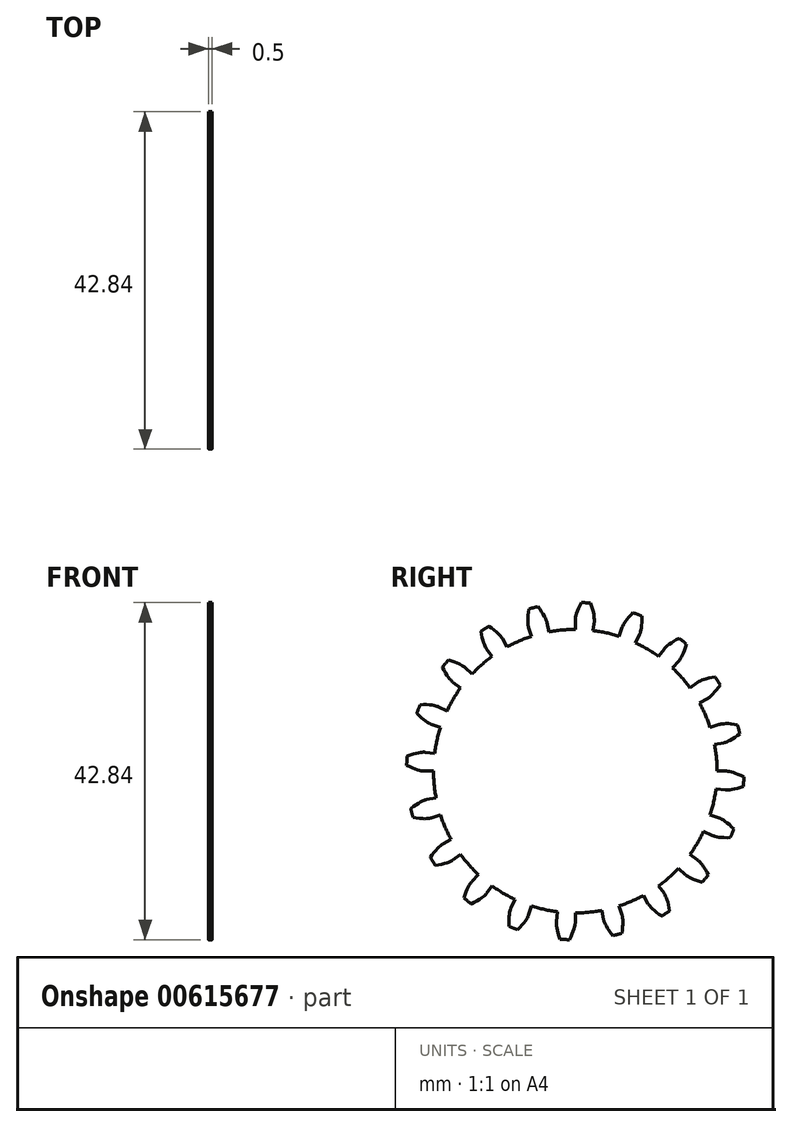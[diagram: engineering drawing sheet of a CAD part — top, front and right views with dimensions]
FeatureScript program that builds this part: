
annotation { "Feature Type Name" : "Feature", "Feature Type Description" : "" }
export const myFeature = defineFeature(function(context is Context, id is Id, definition is map)
    precondition{}
    {
        {
            assignVariable(context, id + "F0", {"name" : "GearThickness", "anyValue" : .5});
        }
        {
            var Q0;
            Q0=qCreatedBy(makeId("Right.planeOp"),FACE);
            var sketch = newSketch(context, id + "F1", { "sketchPlane" : qUnion([Q0])});
            skCircle(sketch, "E0", {"center": v(0, 0) * mm, "radius": 18 * mm});
            skCircle(sketch, "E1", {"center": v(0, 0) * mm, "radius": 19.21 * mm, "construction": true});
            skCircle(sketch, "E2", {"center": v(0, 0) * mm, "radius": 19.84 * mm, "construction": true});
            skCircle(sketch, "E3", {"center": v(0, 0) * mm, "radius": 21.43 * mm});
            skLineSegment(sketch, "E4", {"start": v(0, 0) * mm, "end": v(-19.21, 0) * mm, "construction": true});
            skLineSegment(sketch, "E5.1.0", {"start": v(0, 0) * mm, "end": v(-19.19, 0.96) * mm, "construction": true});
            skLineSegment(sketch, "E5.2.0", {"start": v(0, 0) * mm, "end": v(-19.12, 1.92) * mm, "construction": true});
            skLineSegment(sketch, "E5.3.0", {"start": v(0, 0) * mm, "end": v(-19, 2.87) * mm, "construction": true});
            skLineSegment(sketch, "E5.4.0", {"start": v(0, 0) * mm, "end": v(-18.83, 3.82) * mm, "construction": true});
            skLineSegment(sketch, "E5.5.0", {"start": v(0, 0) * mm, "end": v(-18.61, 4.75) * mm, "construction": true});
            skLineSegment(sketch, "E5.6.0", {"start": v(0, 0) * mm, "end": v(-18.35, 5.68) * mm, "construction": true});
            skLineSegment(sketch, "E5.7.0", {"start": v(0, 0) * mm, "end": v(-18.05, 6.59) * mm, "construction": true});
            skLineSegment(sketch, "E5.8.0", {"start": v(0, 0) * mm, "end": v(-17.7, 7.48) * mm, "construction": true});
            skLineSegment(sketch, "E5.9.0", {"start": v(0, 0) * mm, "end": v(-17.3, 8.36) * mm, "construction": true});
            skLineSegment(sketch, "E5.10.0", {"start": v(0, 0) * mm, "end": v(-16.86, 9.21) * mm, "construction": true});
            skLineSegment(sketch, "E5.11.0", {"start": v(0, 0) * mm, "end": v(-16.38, 10.04) * mm, "construction": true});
            skLineSegment(sketch, "E5.12.0", {"start": v(0, 0) * mm, "end": v(-15.86, 10.85) * mm, "construction": true});
            skLineSegment(sketch, "E5.13.0", {"start": v(0, 0) * mm, "end": v(-15.3, 11.63) * mm, "construction": true});
            skLineSegment(sketch, "E5.14.0", {"start": v(0, 0) * mm, "end": v(-14.7, 12.38) * mm, "construction": true});
            skLineSegment(sketch, "E5.anchor2", {"start": v(0, 0) * mm, "end": v(-14.7, 12.38) * mm, "construction": true});
            skLineSegment(sketch, "E6", {"start": v(-19.19, 0.96) * mm, "end": v(-19.24, 0) * mm, "construction": true});
            skLineSegment(sketch, "E7", {"start": v(-19.12, 1.92) * mm, "end": v(-19.3, 0) * mm, "construction": true});
            skLineSegment(sketch, "E8", {"start": v(-19, 2.87) * mm, "end": v(-19.43, 0.02) * mm, "construction": true});
            skLineSegment(sketch, "E9", {"start": v(-18.61, 4.75) * mm, "end": v(-19.8, 0.1) * mm, "construction": true});
            skLineSegment(sketch, "E10", {"start": v(-18.35, 5.68) * mm, "end": v(-20.06, 0.17) * mm, "construction": true});
            skLineSegment(sketch, "E11", {"start": v(-18.05, 6.59) * mm, "end": v(-20.35, 0.27) * mm, "construction": true});
            skLineSegment(sketch, "E12", {"start": v(-17.7, 7.48) * mm, "end": v(-20.69, 0.4) * mm, "construction": true});
            skLineSegment(sketch, "E13", {"start": v(-17.3, 8.36) * mm, "end": v(-21.06, 0.57) * mm, "construction": true});
            skLineSegment(sketch, "E14", {"start": v(-16.86, 9.21) * mm, "end": v(-21.47, 0.78) * mm, "construction": true});
            skLineSegment(sketch, "E15", {"start": v(-16.38, 10.04) * mm, "end": v(-21.9, 1.03) * mm, "construction": true});
            skLineSegment(sketch, "E16", {"start": v(-18.83, 3.82) * mm, "end": v(-19.6, 0.05) * mm, "construction": true});
            skLineSegment(sketch, "E17", {"start": v(-15.86, 10.85) * mm, "end": v(-22.36, 1.33) * mm, "construction": true});
            skLineSegment(sketch, "E18", {"start": v(-15.3, 11.63) * mm, "end": v(-22.85, 1.69) * mm, "construction": true});
            skLineSegment(sketch, "E19", {"start": v(-14.7, 12.38) * mm, "end": v(-23.36, 2.1) * mm, "construction": true});
            skLineSegment(sketch, "E20", {"start": v(0, 0) * mm, "end": v(-19.17, 1.2) * mm, "construction": true});
            skLineSegment(sketch, "E21", {"start": v(-18, 0) * mm, "end": v(-19.21, 0) * mm});
            skLineSegment(sketch, "E22.MirrorCS", {"start": v(-17.87, 2.26) * mm, "end": v(-19.06, 2.4) * mm});
            skLineSegment(sketch, "E23", {"start": v(-19.21, 0) * mm, "end": v(-19.24, 0) * mm});
            skLineSegment(sketch, "E24", {"start": v(-19.24, 0) * mm, "end": v(-19.3, 0) * mm});
            skLineSegment(sketch, "E25", {"start": v(-19.3, 0) * mm, "end": v(-19.43, 0.02) * mm});
            skLineSegment(sketch, "E26", {"start": v(-19.43, 0.02) * mm, "end": v(-19.6, 0.05) * mm});
            skLineSegment(sketch, "E27", {"start": v(-19.6, 0.05) * mm, "end": v(-19.8, 0.1) * mm});
            skLineSegment(sketch, "E28", {"start": v(-19.8, 0.1) * mm, "end": v(-20.06, 0.17) * mm});
            skLineSegment(sketch, "E29", {"start": v(-20.06, 0.17) * mm, "end": v(-20.35, 0.27) * mm});
            skLineSegment(sketch, "E30", {"start": v(-20.35, 0.27) * mm, "end": v(-20.69, 0.4) * mm});
            skLineSegment(sketch, "E31", {"start": v(-20.69, 0.4) * mm, "end": v(-21.06, 0.57) * mm});
            skLineSegment(sketch, "E32", {"start": v(-21.06, 0.57) * mm, "end": v(-21.47, 0.78) * mm});
            skLineSegment(sketch, "E33", {"start": v(-21.47, 0.78) * mm, "end": v(-21.9, 1.03) * mm});
            skLineSegment(sketch, "E34", {"start": v(-21.9, 1.03) * mm, "end": v(-22.36, 1.33) * mm});
            skLineSegment(sketch, "E35", {"start": v(-22.36, 1.33) * mm, "end": v(-22.85, 1.69) * mm});
            skLineSegment(sketch, "E36", {"start": v(-22.85, 1.69) * mm, "end": v(-23.36, 2.1) * mm});
            skLineSegment(sketch, "E37.MirrorCS", {"start": v(-19.06, 2.4) * mm, "end": v(-19.08, 2.41) * mm});
            skLineSegment(sketch, "E38.MirrorCS", {"start": v(-19.08, 2.41) * mm, "end": v(-19.16, 2.41) * mm});
            skLineSegment(sketch, "E39.MirrorCS", {"start": v(-19.16, 2.41) * mm, "end": v(-19.28, 2.41) * mm});
            skLineSegment(sketch, "E40.MirrorCS", {"start": v(-19.28, 2.41) * mm, "end": v(-19.44, 2.4) * mm});
            skLineSegment(sketch, "E41.MirrorCS", {"start": v(-19.66, 2.38) * mm, "end": v(-19.92, 2.34) * mm});
            skLineSegment(sketch, "E42.MirrorCS", {"start": v(-19.92, 2.34) * mm, "end": v(-20.23, 2.28) * mm});
            skLineSegment(sketch, "E43.MirrorCS", {"start": v(-20.23, 2.28) * mm, "end": v(-20.58, 2.2) * mm});
            skLineSegment(sketch, "E44.MirrorCS", {"start": v(-20.58, 2.2) * mm, "end": v(-20.97, 2.07) * mm});
            skLineSegment(sketch, "E45.MirrorCS", {"start": v(-21.4, 1.92) * mm, "end": v(-21.86, 1.72) * mm});
            skLineSegment(sketch, "E46.MirrorCS", {"start": v(-20.97, 2.07) * mm, "end": v(-21.4, 1.92) * mm});
            skLineSegment(sketch, "E47.MirrorCS", {"start": v(-21.86, 1.72) * mm, "end": v(-22.36, 1.48) * mm});
            skLineSegment(sketch, "E48.MirrorCS", {"start": v(-22.36, 1.48) * mm, "end": v(-22.88, 1.2) * mm});
            skLineSegment(sketch, "E49.MirrorCS", {"start": v(-22.88, 1.2) * mm, "end": v(-23.44, 0.85) * mm});
            skLineSegment(sketch, "E50.MirrorCS", {"start": v(-19.44, 2.4) * mm, "end": v(-19.66, 2.38) * mm});
            skLineSegment(sketch, "E51.1.0", {"start": v(-17.13, -5.56) * mm, "end": v(-18.27, -5.94) * mm});
            skLineSegment(sketch, "E51.1.1", {"start": v(-21.32, -5.12) * mm, "end": v(-21.72, -5.5) * mm});
            skLineSegment(sketch, "E51.1.2", {"start": v(-17.69, -3.37) * mm, "end": v(-18.87, -3.6) * mm});
            skLineSegment(sketch, "E51.1.3", {"start": v(-20.94, -4.79) * mm, "end": v(-21.32, -5.12) * mm});
            skLineSegment(sketch, "E51.1.4", {"start": v(-20.66, -5.9) * mm, "end": v(-21.15, -5.78) * mm});
            skLineSegment(sketch, "E51.1.5", {"start": v(-21.15, -5.78) * mm, "end": v(-21.68, -5.64) * mm});
            skLineSegment(sketch, "E51.1.6", {"start": v(-20.58, -4.5) * mm, "end": v(-20.94, -4.79) * mm});
            skLineSegment(sketch, "E51.1.7", {"start": v(-22.13, -5.94) * mm, "end": v(-22.55, -6.43) * mm});
            skLineSegment(sketch, "E51.1.8", {"start": v(-20.25, -4.27) * mm, "end": v(-20.58, -4.5) * mm});
            skLineSegment(sketch, "E51.1.9", {"start": v(-22.25, -5.46) * mm, "end": v(-22.86, -5.23) * mm});
            skLineSegment(sketch, "E51.1.10", {"start": v(-21.72, -5.5) * mm, "end": v(-22.13, -5.94) * mm});
            skLineSegment(sketch, "E51.1.11", {"start": v(-20.2, -5.96) * mm, "end": v(-20.66, -5.9) * mm});
            skLineSegment(sketch, "E51.1.12", {"start": v(-21.68, -5.64) * mm, "end": v(-22.25, -5.46) * mm});
            skLineSegment(sketch, "E51.1.13", {"start": v(-19.43, -3.8) * mm, "end": v(-19.67, -3.93) * mm});
            skLineSegment(sketch, "E51.1.14", {"start": v(-19.67, -3.93) * mm, "end": v(-19.94, -4.08) * mm});
            skLineSegment(sketch, "E51.1.15", {"start": v(-19.94, -4.08) * mm, "end": v(-20.25, -4.27) * mm});
            skLineSegment(sketch, "E51.1.16", {"start": v(-19.44, -6.03) * mm, "end": v(-19.8, -6) * mm});
            skLineSegment(sketch, "E51.1.17", {"start": v(-19.13, -6.03) * mm, "end": v(-19.44, -6.03) * mm});
            skLineSegment(sketch, "E51.1.18", {"start": v(-19.8, -6) * mm, "end": v(-20.2, -5.96) * mm});
            skLineSegment(sketch, "E51.1.19", {"start": v(-19.24, -3.72) * mm, "end": v(-19.43, -3.8) * mm});
            skLineSegment(sketch, "E51.1.20", {"start": v(-19.08, -3.66) * mm, "end": v(-19.24, -3.72) * mm});
            skLineSegment(sketch, "E51.1.21", {"start": v(-18.86, -6.02) * mm, "end": v(-19.13, -6.03) * mm});
            skLineSegment(sketch, "E51.1.22", {"start": v(-18.65, -6) * mm, "end": v(-18.86, -6.02) * mm});
            skLineSegment(sketch, "E51.1.23", {"start": v(-18.36, -5.96) * mm, "end": v(-18.48, -5.98) * mm});
            skLineSegment(sketch, "E51.1.24", {"start": v(-18.87, -3.6) * mm, "end": v(-18.9, -3.6) * mm});
            skLineSegment(sketch, "E51.1.25", {"start": v(-18.9, -3.6) * mm, "end": v(-18.96, -3.62) * mm});
            skLineSegment(sketch, "E51.1.26", {"start": v(-18.48, -5.98) * mm, "end": v(-18.65, -6) * mm});
            skLineSegment(sketch, "E51.1.27", {"start": v(-18.96, -3.62) * mm, "end": v(-19.08, -3.66) * mm});
            skLineSegment(sketch, "E51.1.28", {"start": v(-18.3, -5.94) * mm, "end": v(-18.36, -5.96) * mm});
            skLineSegment(sketch, "E51.1.29", {"start": v(-18.27, -5.94) * mm, "end": v(-18.3, -5.94) * mm});
            skLineSegment(sketch, "E51.2.0", {"start": v(-14.57, -10.58) * mm, "end": v(-15.54, -11.3) * mm});
            skLineSegment(sketch, "E51.2.1", {"start": v(-18.7, -11.46) * mm, "end": v(-18.96, -11.94) * mm});
            skLineSegment(sketch, "E51.2.2", {"start": v(-15.78, -8.67) * mm, "end": v(-16.84, -9.26) * mm});
            skLineSegment(sketch, "E51.2.3", {"start": v(-18.43, -11.02) * mm, "end": v(-18.7, -11.46) * mm});
            skLineSegment(sketch, "E51.2.4", {"start": v(-17.82, -11.99) * mm, "end": v(-18.33, -12.04) * mm});
            skLineSegment(sketch, "E51.2.5", {"start": v(-18.33, -12.04) * mm, "end": v(-18.88, -12.07) * mm});
            skLineSegment(sketch, "E51.2.6", {"start": v(-18.18, -10.65) * mm, "end": v(-18.43, -11.02) * mm});
            skLineSegment(sketch, "E51.2.7", {"start": v(-19.21, -12.49) * mm, "end": v(-19.46, -13.08) * mm});
            skLineSegment(sketch, "E51.2.8", {"start": v(-17.93, -10.32) * mm, "end": v(-18.18, -10.65) * mm});
            skLineSegment(sketch, "E51.2.9", {"start": v(-19.48, -12.07) * mm, "end": v(-20.13, -12.04) * mm});
            skLineSegment(sketch, "E51.2.10", {"start": v(-18.96, -11.94) * mm, "end": v(-19.21, -12.49) * mm});
            skLineSegment(sketch, "E51.2.11", {"start": v(-17.37, -11.92) * mm, "end": v(-17.82, -11.99) * mm});
            skLineSegment(sketch, "E51.2.12", {"start": v(-18.88, -12.07) * mm, "end": v(-19.48, -12.07) * mm});
            skLineSegment(sketch, "E51.2.13", {"start": v(-17.3, -9.63) * mm, "end": v(-17.5, -9.81) * mm});
            skLineSegment(sketch, "E51.2.14", {"start": v(-17.5, -9.81) * mm, "end": v(-17.7, -10.04) * mm});
            skLineSegment(sketch, "E51.2.15", {"start": v(-17.7, -10.04) * mm, "end": v(-17.93, -10.32) * mm});
            skLineSegment(sketch, "E51.2.16", {"start": v(-16.63, -11.74) * mm, "end": v(-16.97, -11.83) * mm});
            skLineSegment(sketch, "E51.2.17", {"start": v(-16.33, -11.65) * mm, "end": v(-16.63, -11.74) * mm});
            skLineSegment(sketch, "E51.2.18", {"start": v(-16.97, -11.83) * mm, "end": v(-17.37, -11.92) * mm});
            skLineSegment(sketch, "E51.2.19", {"start": v(-17.14, -9.48) * mm, "end": v(-17.3, -9.63) * mm});
            skLineSegment(sketch, "E51.2.20", {"start": v(-17.01, -9.38) * mm, "end": v(-17.14, -9.48) * mm});
            skLineSegment(sketch, "E51.2.21", {"start": v(-16.08, -11.56) * mm, "end": v(-16.33, -11.65) * mm});
            skLineSegment(sketch, "E51.2.22", {"start": v(-15.88, -11.47) * mm, "end": v(-16.08, -11.56) * mm});
            skLineSegment(sketch, "E51.2.23", {"start": v(-15.62, -11.34) * mm, "end": v(-15.73, -11.4) * mm});
            skLineSegment(sketch, "E51.2.24", {"start": v(-16.84, -9.26) * mm, "end": v(-16.86, -9.27) * mm});
            skLineSegment(sketch, "E51.2.25", {"start": v(-16.86, -9.27) * mm, "end": v(-16.92, -9.3) * mm});
            skLineSegment(sketch, "E51.2.26", {"start": v(-15.73, -11.4) * mm, "end": v(-15.88, -11.47) * mm});
            skLineSegment(sketch, "E51.2.27", {"start": v(-16.92, -9.3) * mm, "end": v(-17.01, -9.38) * mm});
            skLineSegment(sketch, "E51.2.28", {"start": v(-15.56, -11.3) * mm, "end": v(-15.62, -11.34) * mm});
            skLineSegment(sketch, "E51.2.29", {"start": v(-15.54, -11.3) * mm, "end": v(-15.56, -11.3) * mm});
            skLineSegment(sketch, "E51.3.0", {"start": v(-10.58, -14.57) * mm, "end": v(-11.3, -15.54) * mm});
            skLineSegment(sketch, "E51.3.1", {"start": v(-14.24, -16.67) * mm, "end": v(-14.34, -17.22) * mm});
            skLineSegment(sketch, "E51.3.2", {"start": v(-12.33, -13.13) * mm, "end": v(-13.15, -14) * mm});
            skLineSegment(sketch, "E51.3.3", {"start": v(-14.12, -16.18) * mm, "end": v(-14.24, -16.67) * mm});
            skLineSegment(sketch, "E51.3.4", {"start": v(-13.25, -16.9) * mm, "end": v(-13.7, -17.11) * mm});
            skLineSegment(sketch, "E51.3.5", {"start": v(-13.7, -17.11) * mm, "end": v(-14.22, -17.3) * mm});
            skLineSegment(sketch, "E51.3.6", {"start": v(-14, -15.74) * mm, "end": v(-14.12, -16.18) * mm});
            skLineSegment(sketch, "E51.3.7", {"start": v(-14.41, -17.81) * mm, "end": v(-14.47, -18.46) * mm});
            skLineSegment(sketch, "E51.3.8", {"start": v(-13.87, -15.36) * mm, "end": v(-14, -15.74) * mm});
            skLineSegment(sketch, "E51.3.9", {"start": v(-14.8, -17.5) * mm, "end": v(-15.42, -17.67) * mm});
            skLineSegment(sketch, "E51.3.10", {"start": v(-14.34, -17.22) * mm, "end": v(-14.41, -17.81) * mm});
            skLineSegment(sketch, "E51.3.11", {"start": v(-12.84, -16.7) * mm, "end": v(-13.25, -16.9) * mm});
            skLineSegment(sketch, "E51.3.12", {"start": v(-14.22, -17.3) * mm, "end": v(-14.8, -17.5) * mm});
            skLineSegment(sketch, "E51.3.13", {"start": v(-13.48, -14.5) * mm, "end": v(-13.6, -14.74) * mm});
            skLineSegment(sketch, "E51.3.14", {"start": v(-13.6, -14.74) * mm, "end": v(-13.73, -15.02) * mm});
            skLineSegment(sketch, "E51.3.15", {"start": v(-13.73, -15.02) * mm, "end": v(-13.87, -15.36) * mm});
            skLineSegment(sketch, "E51.3.16", {"start": v(-12.18, -16.3) * mm, "end": v(-12.49, -16.5) * mm});
            skLineSegment(sketch, "E51.3.17", {"start": v(-11.93, -16.13) * mm, "end": v(-12.18, -16.3) * mm});
            skLineSegment(sketch, "E51.3.18", {"start": v(-12.49, -16.5) * mm, "end": v(-12.84, -16.7) * mm});
            skLineSegment(sketch, "E51.3.19", {"start": v(-13.37, -14.32) * mm, "end": v(-13.48, -14.5) * mm});
            skLineSegment(sketch, "E51.3.20", {"start": v(-13.28, -14.18) * mm, "end": v(-13.37, -14.32) * mm});
            skLineSegment(sketch, "E51.3.21", {"start": v(-11.72, -15.96) * mm, "end": v(-11.93, -16.13) * mm});
            skLineSegment(sketch, "E51.3.22", {"start": v(-11.56, -15.82) * mm, "end": v(-11.72, -15.96) * mm});
            skLineSegment(sketch, "E51.3.23", {"start": v(-11.35, -15.62) * mm, "end": v(-11.44, -15.7) * mm});
            skLineSegment(sketch, "E51.3.24", {"start": v(-13.15, -14) * mm, "end": v(-13.17, -14.02) * mm});
            skLineSegment(sketch, "E51.3.25", {"start": v(-13.17, -14.02) * mm, "end": v(-13.21, -14.08) * mm});
            skLineSegment(sketch, "E51.3.26", {"start": v(-11.44, -15.7) * mm, "end": v(-11.56, -15.82) * mm});
            skLineSegment(sketch, "E51.3.27", {"start": v(-13.21, -14.08) * mm, "end": v(-13.28, -14.18) * mm});
            skLineSegment(sketch, "E51.3.28", {"start": v(-11.3, -15.56) * mm, "end": v(-11.35, -15.62) * mm});
            skLineSegment(sketch, "E51.3.29", {"start": v(-11.3, -15.54) * mm, "end": v(-11.3, -15.56) * mm});
            skLineSegment(sketch, "E51.4.0", {"start": v(-5.56, -17.13) * mm, "end": v(-5.94, -18.27) * mm});
            skLineSegment(sketch, "E51.4.1", {"start": v(-8.39, -20.26) * mm, "end": v(-8.32, -20.8) * mm});
            skLineSegment(sketch, "E51.4.2", {"start": v(-7.67, -16.3) * mm, "end": v(-8.18, -17.38) * mm});
            skLineSegment(sketch, "E51.4.3", {"start": v(-8.43, -19.75) * mm, "end": v(-8.39, -20.26) * mm});
            skLineSegment(sketch, "E51.4.4", {"start": v(-7.38, -20.17) * mm, "end": v(-7.75, -20.51) * mm});
            skLineSegment(sketch, "E51.4.5", {"start": v(-7.75, -20.51) * mm, "end": v(-8.18, -20.86) * mm});
            skLineSegment(sketch, "E51.4.6", {"start": v(-8.45, -19.3) * mm, "end": v(-8.43, -19.75) * mm});
            skLineSegment(sketch, "E51.4.7", {"start": v(-8.2, -21.4) * mm, "end": v(-8.05, -22.02) * mm});
            skLineSegment(sketch, "E51.4.8", {"start": v(-8.44, -18.9) * mm, "end": v(-8.45, -19.3) * mm});
            skLineSegment(sketch, "E51.4.9", {"start": v(-8.66, -21.21) * mm, "end": v(-9.2, -21.57) * mm});
            skLineSegment(sketch, "E51.4.10", {"start": v(-8.32, -20.8) * mm, "end": v(-8.2, -21.4) * mm});
            skLineSegment(sketch, "E51.4.11", {"start": v(-7.05, -19.85) * mm, "end": v(-7.38, -20.17) * mm});
            skLineSegment(sketch, "E51.4.12", {"start": v(-8.18, -20.86) * mm, "end": v(-8.66, -21.21) * mm});
            skLineSegment(sketch, "E51.4.13", {"start": v(-8.34, -17.96) * mm, "end": v(-8.38, -18.22) * mm});
            skLineSegment(sketch, "E51.4.14", {"start": v(-8.38, -18.22) * mm, "end": v(-8.42, -18.53) * mm});
            skLineSegment(sketch, "E51.4.15", {"start": v(-8.42, -18.53) * mm, "end": v(-8.44, -18.9) * mm});
            skLineSegment(sketch, "E51.4.16", {"start": v(-6.55, -19.27) * mm, "end": v(-6.78, -19.55) * mm});
            skLineSegment(sketch, "E51.4.17", {"start": v(-6.36, -19.02) * mm, "end": v(-6.55, -19.27) * mm});
            skLineSegment(sketch, "E51.4.18", {"start": v(-6.78, -19.55) * mm, "end": v(-7.05, -19.85) * mm});
            skLineSegment(sketch, "E51.4.19", {"start": v(-8.3, -17.75) * mm, "end": v(-8.34, -17.96) * mm});
            skLineSegment(sketch, "E51.4.20", {"start": v(-8.25, -17.59) * mm, "end": v(-8.3, -17.75) * mm});
            skLineSegment(sketch, "E51.4.21", {"start": v(-6.21, -18.8) * mm, "end": v(-6.36, -19.02) * mm});
            skLineSegment(sketch, "E51.4.22", {"start": v(-6.1, -18.62) * mm, "end": v(-6.21, -18.8) * mm});
            skLineSegment(sketch, "E51.4.23", {"start": v(-5.97, -18.36) * mm, "end": v(-6.02, -18.47) * mm});
            skLineSegment(sketch, "E51.4.24", {"start": v(-8.18, -17.38) * mm, "end": v(-8.19, -17.4) * mm});
            skLineSegment(sketch, "E51.4.25", {"start": v(-8.19, -17.4) * mm, "end": v(-8.21, -17.47) * mm});
            skLineSegment(sketch, "E51.4.26", {"start": v(-6.02, -18.47) * mm, "end": v(-6.1, -18.62) * mm});
            skLineSegment(sketch, "E51.4.27", {"start": v(-8.21, -17.47) * mm, "end": v(-8.25, -17.59) * mm});
            skLineSegment(sketch, "E51.4.28", {"start": v(-5.94, -18.3) * mm, "end": v(-5.97, -18.36) * mm});
            skLineSegment(sketch, "E51.4.29", {"start": v(-5.94, -18.27) * mm, "end": v(-5.94, -18.3) * mm});
            skLineSegment(sketch, "E51.5.0", {"start": v(0, -18) * mm, "end": v(0, -19.21) * mm});
            skLineSegment(sketch, "E51.5.1", {"start": v(-1.72, -21.86) * mm, "end": v(-1.48, -22.36) * mm});
            skLineSegment(sketch, "E51.5.2", {"start": v(-2.26, -17.87) * mm, "end": v(-2.4, -19.06) * mm});
            skLineSegment(sketch, "E51.5.3", {"start": v(-1.92, -21.4) * mm, "end": v(-1.72, -21.86) * mm});
            skLineSegment(sketch, "E51.5.4", {"start": v(-0.78, -21.47) * mm, "end": v(-1.03, -21.9) * mm});
            skLineSegment(sketch, "E51.5.5", {"start": v(-1.03, -21.9) * mm, "end": v(-1.33, -22.36) * mm});
            skLineSegment(sketch, "E51.5.6", {"start": v(-2.07, -20.97) * mm, "end": v(-1.92, -21.4) * mm});
            skLineSegment(sketch, "E51.5.7", {"start": v(-1.2, -22.88) * mm, "end": v(-0.85, -23.44) * mm});
            skLineSegment(sketch, "E51.5.8", {"start": v(-2.2, -20.58) * mm, "end": v(-2.07, -20.97) * mm});
            skLineSegment(sketch, "E51.5.9", {"start": v(-1.69, -22.85) * mm, "end": v(-2.1, -23.36) * mm});
            skLineSegment(sketch, "E51.5.10", {"start": v(-1.48, -22.36) * mm, "end": v(-1.2, -22.88) * mm});
            skLineSegment(sketch, "E51.5.11", {"start": v(-0.57, -21.06) * mm, "end": v(-0.78, -21.47) * mm});
            skLineSegment(sketch, "E51.5.12", {"start": v(-1.33, -22.36) * mm, "end": v(-1.69, -22.85) * mm});
            skLineSegment(sketch, "E51.5.13", {"start": v(-2.38, -19.66) * mm, "end": v(-2.34, -19.92) * mm});
            skLineSegment(sketch, "E51.5.14", {"start": v(-2.34, -19.92) * mm, "end": v(-2.28, -20.23) * mm});
            skLineSegment(sketch, "E51.5.15", {"start": v(-2.28, -20.23) * mm, "end": v(-2.2, -20.58) * mm});
            skLineSegment(sketch, "E51.5.16", {"start": v(-0.27, -20.35) * mm, "end": v(-0.4, -20.69) * mm});
            skLineSegment(sketch, "E51.5.17", {"start": v(-0.17, -20.06) * mm, "end": v(-0.27, -20.35) * mm});
            skLineSegment(sketch, "E51.5.18", {"start": v(-0.4, -20.69) * mm, "end": v(-0.57, -21.06) * mm});
            skLineSegment(sketch, "E51.5.19", {"start": v(-2.4, -19.44) * mm, "end": v(-2.38, -19.66) * mm});
            skLineSegment(sketch, "E51.5.20", {"start": v(-2.41, -19.28) * mm, "end": v(-2.4, -19.44) * mm});
            skLineSegment(sketch, "E51.5.21", {"start": v(-0.1, -19.8) * mm, "end": v(-0.17, -20.06) * mm});
            skLineSegment(sketch, "E51.5.22", {"start": v(-0.05, -19.6) * mm, "end": v(-0.1, -19.8) * mm});
            skLineSegment(sketch, "E51.5.23", {"start": v(0, -19.3) * mm, "end": v(-0.02, -19.43) * mm});
            skLineSegment(sketch, "E51.5.24", {"start": v(-2.4, -19.06) * mm, "end": v(-2.41, -19.08) * mm});
            skLineSegment(sketch, "E51.5.25", {"start": v(-2.41, -19.08) * mm, "end": v(-2.41, -19.16) * mm});
            skLineSegment(sketch, "E51.5.26", {"start": v(-0.02, -19.43) * mm, "end": v(-0.05, -19.6) * mm});
            skLineSegment(sketch, "E51.5.27", {"start": v(-2.41, -19.16) * mm, "end": v(-2.41, -19.28) * mm});
            skLineSegment(sketch, "E51.5.28", {"start": v(0, -19.24) * mm, "end": v(0, -19.3) * mm});
            skLineSegment(sketch, "E51.5.29", {"start": v(0, -19.21) * mm, "end": v(0, -19.24) * mm});
            skLineSegment(sketch, "E51.6.0", {"start": v(5.56, -17.13) * mm, "end": v(5.94, -18.27) * mm});
            skLineSegment(sketch, "E51.6.1", {"start": v(5.12, -21.32) * mm, "end": v(5.5, -21.72) * mm});
            skLineSegment(sketch, "E51.6.2", {"start": v(3.37, -17.69) * mm, "end": v(3.6, -18.87) * mm});
            skLineSegment(sketch, "E51.6.3", {"start": v(4.79, -20.94) * mm, "end": v(5.12, -21.32) * mm});
            skLineSegment(sketch, "E51.6.4", {"start": v(5.9, -20.66) * mm, "end": v(5.78, -21.15) * mm});
            skLineSegment(sketch, "E51.6.5", {"start": v(5.78, -21.15) * mm, "end": v(5.64, -21.68) * mm});
            skLineSegment(sketch, "E51.6.6", {"start": v(4.5, -20.58) * mm, "end": v(4.79, -20.94) * mm});
            skLineSegment(sketch, "E51.6.7", {"start": v(5.94, -22.13) * mm, "end": v(6.43, -22.55) * mm});
            skLineSegment(sketch, "E51.6.8", {"start": v(4.27, -20.25) * mm, "end": v(4.5, -20.58) * mm});
            skLineSegment(sketch, "E51.6.9", {"start": v(5.46, -22.25) * mm, "end": v(5.23, -22.86) * mm});
            skLineSegment(sketch, "E51.6.10", {"start": v(5.5, -21.72) * mm, "end": v(5.94, -22.13) * mm});
            skLineSegment(sketch, "E51.6.11", {"start": v(5.96, -20.2) * mm, "end": v(5.9, -20.66) * mm});
            skLineSegment(sketch, "E51.6.12", {"start": v(5.64, -21.68) * mm, "end": v(5.46, -22.25) * mm});
            skLineSegment(sketch, "E51.6.13", {"start": v(3.8, -19.43) * mm, "end": v(3.93, -19.67) * mm});
            skLineSegment(sketch, "E51.6.14", {"start": v(3.93, -19.67) * mm, "end": v(4.08, -19.94) * mm});
            skLineSegment(sketch, "E51.6.15", {"start": v(4.08, -19.94) * mm, "end": v(4.27, -20.25) * mm});
            skLineSegment(sketch, "E51.6.16", {"start": v(6.03, -19.44) * mm, "end": v(6, -19.8) * mm});
            skLineSegment(sketch, "E51.6.17", {"start": v(6.03, -19.13) * mm, "end": v(6.03, -19.44) * mm});
            skLineSegment(sketch, "E51.6.18", {"start": v(6, -19.8) * mm, "end": v(5.96, -20.2) * mm});
            skLineSegment(sketch, "E51.6.19", {"start": v(3.72, -19.24) * mm, "end": v(3.8, -19.43) * mm});
            skLineSegment(sketch, "E51.6.20", {"start": v(3.66, -19.08) * mm, "end": v(3.72, -19.24) * mm});
            skLineSegment(sketch, "E51.6.21", {"start": v(6.02, -18.86) * mm, "end": v(6.03, -19.13) * mm});
            skLineSegment(sketch, "E51.6.22", {"start": v(6, -18.65) * mm, "end": v(6.02, -18.86) * mm});
            skLineSegment(sketch, "E51.6.23", {"start": v(5.96, -18.36) * mm, "end": v(5.98, -18.48) * mm});
            skLineSegment(sketch, "E51.6.24", {"start": v(3.6, -18.87) * mm, "end": v(3.6, -18.9) * mm});
            skLineSegment(sketch, "E51.6.25", {"start": v(3.6, -18.9) * mm, "end": v(3.62, -18.96) * mm});
            skLineSegment(sketch, "E51.6.26", {"start": v(5.98, -18.48) * mm, "end": v(6, -18.65) * mm});
            skLineSegment(sketch, "E51.6.27", {"start": v(3.62, -18.96) * mm, "end": v(3.66, -19.08) * mm});
            skLineSegment(sketch, "E51.6.28", {"start": v(5.94, -18.3) * mm, "end": v(5.96, -18.36) * mm});
            skLineSegment(sketch, "E51.6.29", {"start": v(5.94, -18.27) * mm, "end": v(5.94, -18.3) * mm});
            skLineSegment(sketch, "E51.7.0", {"start": v(10.58, -14.57) * mm, "end": v(11.3, -15.54) * mm});
            skLineSegment(sketch, "E51.7.1", {"start": v(11.46, -18.7) * mm, "end": v(11.94, -18.96) * mm});
            skLineSegment(sketch, "E51.7.2", {"start": v(8.67, -15.78) * mm, "end": v(9.26, -16.84) * mm});
            skLineSegment(sketch, "E51.7.3", {"start": v(11.02, -18.43) * mm, "end": v(11.46, -18.7) * mm});
            skLineSegment(sketch, "E51.7.4", {"start": v(11.99, -17.82) * mm, "end": v(12.04, -18.33) * mm});
            skLineSegment(sketch, "E51.7.5", {"start": v(12.04, -18.33) * mm, "end": v(12.07, -18.88) * mm});
            skLineSegment(sketch, "E51.7.6", {"start": v(10.65, -18.18) * mm, "end": v(11.02, -18.43) * mm});
            skLineSegment(sketch, "E51.7.7", {"start": v(12.49, -19.21) * mm, "end": v(13.08, -19.46) * mm});
            skLineSegment(sketch, "E51.7.8", {"start": v(10.32, -17.93) * mm, "end": v(10.65, -18.18) * mm});
            skLineSegment(sketch, "E51.7.9", {"start": v(12.07, -19.48) * mm, "end": v(12.04, -20.13) * mm});
            skLineSegment(sketch, "E51.7.10", {"start": v(11.94, -18.96) * mm, "end": v(12.49, -19.21) * mm});
            skLineSegment(sketch, "E51.7.11", {"start": v(11.92, -17.37) * mm, "end": v(11.99, -17.82) * mm});
            skLineSegment(sketch, "E51.7.12", {"start": v(12.07, -18.88) * mm, "end": v(12.07, -19.48) * mm});
            skLineSegment(sketch, "E51.7.13", {"start": v(9.63, -17.3) * mm, "end": v(9.81, -17.5) * mm});
            skLineSegment(sketch, "E51.7.14", {"start": v(9.81, -17.5) * mm, "end": v(10.04, -17.7) * mm});
            skLineSegment(sketch, "E51.7.15", {"start": v(10.04, -17.7) * mm, "end": v(10.32, -17.93) * mm});
            skLineSegment(sketch, "E51.7.16", {"start": v(11.74, -16.63) * mm, "end": v(11.83, -16.97) * mm});
            skLineSegment(sketch, "E51.7.17", {"start": v(11.65, -16.33) * mm, "end": v(11.74, -16.63) * mm});
            skLineSegment(sketch, "E51.7.18", {"start": v(11.83, -16.97) * mm, "end": v(11.92, -17.37) * mm});
            skLineSegment(sketch, "E51.7.19", {"start": v(9.48, -17.14) * mm, "end": v(9.63, -17.3) * mm});
            skLineSegment(sketch, "E51.7.20", {"start": v(9.38, -17.01) * mm, "end": v(9.48, -17.14) * mm});
            skLineSegment(sketch, "E51.7.21", {"start": v(11.56, -16.08) * mm, "end": v(11.65, -16.33) * mm});
            skLineSegment(sketch, "E51.7.22", {"start": v(11.47, -15.88) * mm, "end": v(11.56, -16.08) * mm});
            skLineSegment(sketch, "E51.7.23", {"start": v(11.34, -15.62) * mm, "end": v(11.4, -15.73) * mm});
            skLineSegment(sketch, "E51.7.24", {"start": v(9.26, -16.84) * mm, "end": v(9.27, -16.86) * mm});
            skLineSegment(sketch, "E51.7.25", {"start": v(9.27, -16.86) * mm, "end": v(9.3, -16.92) * mm});
            skLineSegment(sketch, "E51.7.26", {"start": v(11.4, -15.73) * mm, "end": v(11.47, -15.88) * mm});
            skLineSegment(sketch, "E51.7.27", {"start": v(9.3, -16.92) * mm, "end": v(9.38, -17.01) * mm});
            skLineSegment(sketch, "E51.7.28", {"start": v(11.3, -15.56) * mm, "end": v(11.34, -15.62) * mm});
            skLineSegment(sketch, "E51.7.29", {"start": v(11.3, -15.54) * mm, "end": v(11.3, -15.56) * mm});
            skLineSegment(sketch, "E51.8.0", {"start": v(14.57, -10.58) * mm, "end": v(15.54, -11.3) * mm});
            skLineSegment(sketch, "E51.8.1", {"start": v(16.67, -14.24) * mm, "end": v(17.22, -14.34) * mm});
            skLineSegment(sketch, "E51.8.2", {"start": v(13.13, -12.33) * mm, "end": v(14, -13.15) * mm});
            skLineSegment(sketch, "E51.8.3", {"start": v(16.18, -14.12) * mm, "end": v(16.67, -14.24) * mm});
            skLineSegment(sketch, "E51.8.4", {"start": v(16.9, -13.25) * mm, "end": v(17.11, -13.7) * mm});
            skLineSegment(sketch, "E51.8.5", {"start": v(17.11, -13.7) * mm, "end": v(17.3, -14.22) * mm});
            skLineSegment(sketch, "E51.8.6", {"start": v(15.74, -14) * mm, "end": v(16.18, -14.12) * mm});
            skLineSegment(sketch, "E51.8.7", {"start": v(17.81, -14.41) * mm, "end": v(18.46, -14.47) * mm});
            skLineSegment(sketch, "E51.8.8", {"start": v(15.36, -13.87) * mm, "end": v(15.74, -14) * mm});
            skLineSegment(sketch, "E51.8.9", {"start": v(17.5, -14.8) * mm, "end": v(17.67, -15.42) * mm});
            skLineSegment(sketch, "E51.8.10", {"start": v(17.22, -14.34) * mm, "end": v(17.81, -14.41) * mm});
            skLineSegment(sketch, "E51.8.11", {"start": v(16.7, -12.84) * mm, "end": v(16.9, -13.25) * mm});
            skLineSegment(sketch, "E51.8.12", {"start": v(17.3, -14.22) * mm, "end": v(17.5, -14.8) * mm});
            skLineSegment(sketch, "E51.8.13", {"start": v(14.5, -13.48) * mm, "end": v(14.74, -13.6) * mm});
            skLineSegment(sketch, "E51.8.14", {"start": v(14.74, -13.6) * mm, "end": v(15.02, -13.73) * mm});
            skLineSegment(sketch, "E51.8.15", {"start": v(15.02, -13.73) * mm, "end": v(15.36, -13.87) * mm});
            skLineSegment(sketch, "E51.8.16", {"start": v(16.3, -12.18) * mm, "end": v(16.5, -12.49) * mm});
            skLineSegment(sketch, "E51.8.17", {"start": v(16.13, -11.93) * mm, "end": v(16.3, -12.18) * mm});
            skLineSegment(sketch, "E51.8.18", {"start": v(16.5, -12.49) * mm, "end": v(16.7, -12.84) * mm});
            skLineSegment(sketch, "E51.8.19", {"start": v(14.32, -13.37) * mm, "end": v(14.5, -13.48) * mm});
            skLineSegment(sketch, "E51.8.20", {"start": v(14.18, -13.28) * mm, "end": v(14.32, -13.37) * mm});
            skLineSegment(sketch, "E51.8.21", {"start": v(15.96, -11.72) * mm, "end": v(16.13, -11.93) * mm});
            skLineSegment(sketch, "E51.8.22", {"start": v(15.82, -11.56) * mm, "end": v(15.96, -11.72) * mm});
            skLineSegment(sketch, "E51.8.23", {"start": v(15.62, -11.35) * mm, "end": v(15.7, -11.44) * mm});
            skLineSegment(sketch, "E51.8.24", {"start": v(14, -13.15) * mm, "end": v(14.02, -13.17) * mm});
            skLineSegment(sketch, "E51.8.25", {"start": v(14.02, -13.17) * mm, "end": v(14.08, -13.21) * mm});
            skLineSegment(sketch, "E51.8.26", {"start": v(15.7, -11.44) * mm, "end": v(15.82, -11.56) * mm});
            skLineSegment(sketch, "E51.8.27", {"start": v(14.08, -13.21) * mm, "end": v(14.18, -13.28) * mm});
            skLineSegment(sketch, "E51.8.28", {"start": v(15.56, -11.3) * mm, "end": v(15.62, -11.35) * mm});
            skLineSegment(sketch, "E51.8.29", {"start": v(15.54, -11.3) * mm, "end": v(15.56, -11.3) * mm});
            skLineSegment(sketch, "E51.9.0", {"start": v(17.13, -5.56) * mm, "end": v(18.27, -5.94) * mm});
            skLineSegment(sketch, "E51.9.1", {"start": v(20.26, -8.39) * mm, "end": v(20.8, -8.32) * mm});
            skLineSegment(sketch, "E51.9.2", {"start": v(16.3, -7.67) * mm, "end": v(17.38, -8.18) * mm});
            skLineSegment(sketch, "E51.9.3", {"start": v(19.75, -8.43) * mm, "end": v(20.26, -8.39) * mm});
            skLineSegment(sketch, "E51.9.4", {"start": v(20.17, -7.38) * mm, "end": v(20.51, -7.75) * mm});
            skLineSegment(sketch, "E51.9.5", {"start": v(20.51, -7.75) * mm, "end": v(20.86, -8.18) * mm});
            skLineSegment(sketch, "E51.9.6", {"start": v(19.3, -8.45) * mm, "end": v(19.75, -8.43) * mm});
            skLineSegment(sketch, "E51.9.7", {"start": v(21.4, -8.2) * mm, "end": v(22.02, -8.05) * mm});
            skLineSegment(sketch, "E51.9.8", {"start": v(18.9, -8.44) * mm, "end": v(19.3, -8.45) * mm});
            skLineSegment(sketch, "E51.9.9", {"start": v(21.21, -8.66) * mm, "end": v(21.57, -9.2) * mm});
            skLineSegment(sketch, "E51.9.10", {"start": v(20.8, -8.32) * mm, "end": v(21.4, -8.2) * mm});
            skLineSegment(sketch, "E51.9.11", {"start": v(19.85, -7.05) * mm, "end": v(20.17, -7.38) * mm});
            skLineSegment(sketch, "E51.9.12", {"start": v(20.86, -8.18) * mm, "end": v(21.21, -8.66) * mm});
            skLineSegment(sketch, "E51.9.13", {"start": v(17.96, -8.34) * mm, "end": v(18.22, -8.38) * mm});
            skLineSegment(sketch, "E51.9.14", {"start": v(18.22, -8.38) * mm, "end": v(18.53, -8.42) * mm});
            skLineSegment(sketch, "E51.9.15", {"start": v(18.53, -8.42) * mm, "end": v(18.9, -8.44) * mm});
            skLineSegment(sketch, "E51.9.16", {"start": v(19.27, -6.55) * mm, "end": v(19.55, -6.78) * mm});
            skLineSegment(sketch, "E51.9.17", {"start": v(19.02, -6.36) * mm, "end": v(19.27, -6.55) * mm});
            skLineSegment(sketch, "E51.9.18", {"start": v(19.55, -6.78) * mm, "end": v(19.85, -7.05) * mm});
            skLineSegment(sketch, "E51.9.19", {"start": v(17.75, -8.3) * mm, "end": v(17.96, -8.34) * mm});
            skLineSegment(sketch, "E51.9.20", {"start": v(17.59, -8.25) * mm, "end": v(17.75, -8.3) * mm});
            skLineSegment(sketch, "E51.9.21", {"start": v(18.8, -6.21) * mm, "end": v(19.02, -6.36) * mm});
            skLineSegment(sketch, "E51.9.22", {"start": v(18.62, -6.1) * mm, "end": v(18.8, -6.21) * mm});
            skLineSegment(sketch, "E51.9.23", {"start": v(18.36, -5.97) * mm, "end": v(18.47, -6.02) * mm});
            skLineSegment(sketch, "E51.9.24", {"start": v(17.38, -8.18) * mm, "end": v(17.4, -8.19) * mm});
            skLineSegment(sketch, "E51.9.25", {"start": v(17.4, -8.19) * mm, "end": v(17.47, -8.21) * mm});
            skLineSegment(sketch, "E51.9.26", {"start": v(18.47, -6.02) * mm, "end": v(18.62, -6.1) * mm});
            skLineSegment(sketch, "E51.9.27", {"start": v(17.47, -8.21) * mm, "end": v(17.59, -8.25) * mm});
            skLineSegment(sketch, "E51.9.28", {"start": v(18.3, -5.94) * mm, "end": v(18.36, -5.97) * mm});
            skLineSegment(sketch, "E51.9.29", {"start": v(18.27, -5.94) * mm, "end": v(18.3, -5.94) * mm});
            skLineSegment(sketch, "E51.10.0", {"start": v(18, 0) * mm, "end": v(19.21, 0) * mm});
            skLineSegment(sketch, "E51.10.1", {"start": v(21.86, -1.72) * mm, "end": v(22.36, -1.48) * mm});
            skLineSegment(sketch, "E51.10.2", {"start": v(17.87, -2.26) * mm, "end": v(19.06, -2.4) * mm});
            skLineSegment(sketch, "E51.10.3", {"start": v(21.4, -1.92) * mm, "end": v(21.86, -1.72) * mm});
            skLineSegment(sketch, "E51.10.4", {"start": v(21.47, -0.78) * mm, "end": v(21.9, -1.03) * mm});
            skLineSegment(sketch, "E51.10.5", {"start": v(21.9, -1.03) * mm, "end": v(22.36, -1.33) * mm});
            skLineSegment(sketch, "E51.10.6", {"start": v(20.97, -2.07) * mm, "end": v(21.4, -1.92) * mm});
            skLineSegment(sketch, "E51.10.7", {"start": v(22.88, -1.2) * mm, "end": v(23.44, -0.85) * mm});
            skLineSegment(sketch, "E51.10.8", {"start": v(20.58, -2.2) * mm, "end": v(20.97, -2.07) * mm});
            skLineSegment(sketch, "E51.10.9", {"start": v(22.85, -1.69) * mm, "end": v(23.36, -2.1) * mm});
            skLineSegment(sketch, "E51.10.10", {"start": v(22.36, -1.48) * mm, "end": v(22.88, -1.2) * mm});
            skLineSegment(sketch, "E51.10.11", {"start": v(21.06, -0.57) * mm, "end": v(21.47, -0.78) * mm});
            skLineSegment(sketch, "E51.10.12", {"start": v(22.36, -1.33) * mm, "end": v(22.85, -1.69) * mm});
            skLineSegment(sketch, "E51.10.13", {"start": v(19.66, -2.38) * mm, "end": v(19.92, -2.34) * mm});
            skLineSegment(sketch, "E51.10.14", {"start": v(19.92, -2.34) * mm, "end": v(20.23, -2.28) * mm});
            skLineSegment(sketch, "E51.10.15", {"start": v(20.23, -2.28) * mm, "end": v(20.58, -2.2) * mm});
            skLineSegment(sketch, "E51.10.16", {"start": v(20.35, -0.27) * mm, "end": v(20.69, -0.4) * mm});
            skLineSegment(sketch, "E51.10.17", {"start": v(20.06, -0.17) * mm, "end": v(20.35, -0.27) * mm});
            skLineSegment(sketch, "E51.10.18", {"start": v(20.69, -0.4) * mm, "end": v(21.06, -0.57) * mm});
            skLineSegment(sketch, "E51.10.19", {"start": v(19.44, -2.4) * mm, "end": v(19.66, -2.38) * mm});
            skLineSegment(sketch, "E51.10.20", {"start": v(19.28, -2.41) * mm, "end": v(19.44, -2.4) * mm});
            skLineSegment(sketch, "E51.10.21", {"start": v(19.8, -0.1) * mm, "end": v(20.06, -0.17) * mm});
            skLineSegment(sketch, "E51.10.22", {"start": v(19.6, -0.05) * mm, "end": v(19.8, -0.1) * mm});
            skLineSegment(sketch, "E51.10.23", {"start": v(19.3, 0) * mm, "end": v(19.43, -0.02) * mm});
            skLineSegment(sketch, "E51.10.24", {"start": v(19.06, -2.4) * mm, "end": v(19.08, -2.41) * mm});
            skLineSegment(sketch, "E51.10.25", {"start": v(19.08, -2.41) * mm, "end": v(19.16, -2.41) * mm});
            skLineSegment(sketch, "E51.10.26", {"start": v(19.43, -0.02) * mm, "end": v(19.6, -0.05) * mm});
            skLineSegment(sketch, "E51.10.27", {"start": v(19.16, -2.41) * mm, "end": v(19.28, -2.41) * mm});
            skLineSegment(sketch, "E51.10.28", {"start": v(19.24, 0) * mm, "end": v(19.3, 0) * mm});
            skLineSegment(sketch, "E51.10.29", {"start": v(19.21, 0) * mm, "end": v(19.24, 0) * mm});
            skLineSegment(sketch, "E51.11.0", {"start": v(17.13, 5.56) * mm, "end": v(18.27, 5.94) * mm});
            skLineSegment(sketch, "E51.11.1", {"start": v(21.32, 5.12) * mm, "end": v(21.72, 5.5) * mm});
            skLineSegment(sketch, "E51.11.2", {"start": v(17.69, 3.37) * mm, "end": v(18.87, 3.6) * mm});
            skLineSegment(sketch, "E51.11.3", {"start": v(20.94, 4.79) * mm, "end": v(21.32, 5.12) * mm});
            skLineSegment(sketch, "E51.11.4", {"start": v(20.66, 5.9) * mm, "end": v(21.15, 5.78) * mm});
            skLineSegment(sketch, "E51.11.5", {"start": v(21.15, 5.78) * mm, "end": v(21.68, 5.64) * mm});
            skLineSegment(sketch, "E51.11.6", {"start": v(20.58, 4.5) * mm, "end": v(20.94, 4.79) * mm});
            skLineSegment(sketch, "E51.11.7", {"start": v(22.13, 5.94) * mm, "end": v(22.55, 6.43) * mm});
            skLineSegment(sketch, "E51.11.8", {"start": v(20.25, 4.27) * mm, "end": v(20.58, 4.5) * mm});
            skLineSegment(sketch, "E51.11.9", {"start": v(22.25, 5.46) * mm, "end": v(22.86, 5.23) * mm});
            skLineSegment(sketch, "E51.11.10", {"start": v(21.72, 5.5) * mm, "end": v(22.13, 5.94) * mm});
            skLineSegment(sketch, "E51.11.11", {"start": v(20.2, 5.96) * mm, "end": v(20.66, 5.9) * mm});
            skLineSegment(sketch, "E51.11.12", {"start": v(21.68, 5.64) * mm, "end": v(22.25, 5.46) * mm});
            skLineSegment(sketch, "E51.11.13", {"start": v(19.43, 3.8) * mm, "end": v(19.67, 3.93) * mm});
            skLineSegment(sketch, "E51.11.14", {"start": v(19.67, 3.93) * mm, "end": v(19.94, 4.08) * mm});
            skLineSegment(sketch, "E51.11.15", {"start": v(19.94, 4.08) * mm, "end": v(20.25, 4.27) * mm});
            skLineSegment(sketch, "E51.11.16", {"start": v(19.44, 6.03) * mm, "end": v(19.8, 6) * mm});
            skLineSegment(sketch, "E51.11.17", {"start": v(19.13, 6.03) * mm, "end": v(19.44, 6.03) * mm});
            skLineSegment(sketch, "E51.11.18", {"start": v(19.8, 6) * mm, "end": v(20.2, 5.96) * mm});
            skLineSegment(sketch, "E51.11.19", {"start": v(19.24, 3.72) * mm, "end": v(19.43, 3.8) * mm});
            skLineSegment(sketch, "E51.11.20", {"start": v(19.08, 3.66) * mm, "end": v(19.24, 3.72) * mm});
            skLineSegment(sketch, "E51.11.21", {"start": v(18.86, 6.02) * mm, "end": v(19.13, 6.03) * mm});
            skLineSegment(sketch, "E51.11.22", {"start": v(18.65, 6) * mm, "end": v(18.86, 6.02) * mm});
            skLineSegment(sketch, "E51.11.23", {"start": v(18.36, 5.96) * mm, "end": v(18.48, 5.98) * mm});
            skLineSegment(sketch, "E51.11.24", {"start": v(18.87, 3.6) * mm, "end": v(18.9, 3.6) * mm});
            skLineSegment(sketch, "E51.11.25", {"start": v(18.9, 3.6) * mm, "end": v(18.96, 3.62) * mm});
            skLineSegment(sketch, "E51.11.26", {"start": v(18.48, 5.98) * mm, "end": v(18.65, 6) * mm});
            skLineSegment(sketch, "E51.11.27", {"start": v(18.96, 3.62) * mm, "end": v(19.08, 3.66) * mm});
            skLineSegment(sketch, "E51.11.28", {"start": v(18.3, 5.94) * mm, "end": v(18.36, 5.96) * mm});
            skLineSegment(sketch, "E51.11.29", {"start": v(18.27, 5.94) * mm, "end": v(18.3, 5.94) * mm});
            skLineSegment(sketch, "E51.12.0", {"start": v(14.57, 10.58) * mm, "end": v(15.54, 11.3) * mm});
            skLineSegment(sketch, "E51.12.1", {"start": v(18.7, 11.46) * mm, "end": v(18.96, 11.94) * mm});
            skLineSegment(sketch, "E51.12.2", {"start": v(15.78, 8.67) * mm, "end": v(16.84, 9.26) * mm});
            skLineSegment(sketch, "E51.12.3", {"start": v(18.43, 11.02) * mm, "end": v(18.7, 11.46) * mm});
            skLineSegment(sketch, "E51.12.4", {"start": v(17.82, 11.99) * mm, "end": v(18.33, 12.04) * mm});
            skLineSegment(sketch, "E51.12.5", {"start": v(18.33, 12.04) * mm, "end": v(18.88, 12.07) * mm});
            skLineSegment(sketch, "E51.12.6", {"start": v(18.18, 10.65) * mm, "end": v(18.43, 11.02) * mm});
            skLineSegment(sketch, "E51.12.7", {"start": v(19.21, 12.49) * mm, "end": v(19.46, 13.08) * mm});
            skLineSegment(sketch, "E51.12.8", {"start": v(17.93, 10.32) * mm, "end": v(18.18, 10.65) * mm});
            skLineSegment(sketch, "E51.12.9", {"start": v(19.48, 12.07) * mm, "end": v(20.13, 12.04) * mm});
            skLineSegment(sketch, "E51.12.10", {"start": v(18.96, 11.94) * mm, "end": v(19.21, 12.49) * mm});
            skLineSegment(sketch, "E51.12.11", {"start": v(17.37, 11.92) * mm, "end": v(17.82, 11.99) * mm});
            skLineSegment(sketch, "E51.12.12", {"start": v(18.88, 12.07) * mm, "end": v(19.48, 12.07) * mm});
            skLineSegment(sketch, "E51.12.13", {"start": v(17.3, 9.63) * mm, "end": v(17.5, 9.81) * mm});
            skLineSegment(sketch, "E51.12.14", {"start": v(17.5, 9.81) * mm, "end": v(17.7, 10.04) * mm});
            skLineSegment(sketch, "E51.12.15", {"start": v(17.7, 10.04) * mm, "end": v(17.93, 10.32) * mm});
            skLineSegment(sketch, "E51.12.16", {"start": v(16.63, 11.74) * mm, "end": v(16.97, 11.83) * mm});
            skLineSegment(sketch, "E51.12.17", {"start": v(16.33, 11.65) * mm, "end": v(16.63, 11.74) * mm});
            skLineSegment(sketch, "E51.12.18", {"start": v(16.97, 11.83) * mm, "end": v(17.37, 11.92) * mm});
            skLineSegment(sketch, "E51.12.19", {"start": v(17.14, 9.48) * mm, "end": v(17.3, 9.63) * mm});
            skLineSegment(sketch, "E51.12.20", {"start": v(17.01, 9.38) * mm, "end": v(17.14, 9.48) * mm});
            skLineSegment(sketch, "E51.12.21", {"start": v(16.08, 11.56) * mm, "end": v(16.33, 11.65) * mm});
            skLineSegment(sketch, "E51.12.22", {"start": v(15.88, 11.47) * mm, "end": v(16.08, 11.56) * mm});
            skLineSegment(sketch, "E51.12.23", {"start": v(15.62, 11.34) * mm, "end": v(15.73, 11.4) * mm});
            skLineSegment(sketch, "E51.12.24", {"start": v(16.84, 9.26) * mm, "end": v(16.86, 9.27) * mm});
            skLineSegment(sketch, "E51.12.25", {"start": v(16.86, 9.27) * mm, "end": v(16.92, 9.3) * mm});
            skLineSegment(sketch, "E51.12.26", {"start": v(15.73, 11.4) * mm, "end": v(15.88, 11.47) * mm});
            skLineSegment(sketch, "E51.12.27", {"start": v(16.92, 9.3) * mm, "end": v(17.01, 9.38) * mm});
            skLineSegment(sketch, "E51.12.28", {"start": v(15.56, 11.3) * mm, "end": v(15.62, 11.34) * mm});
            skLineSegment(sketch, "E51.12.29", {"start": v(15.54, 11.3) * mm, "end": v(15.56, 11.3) * mm});
            skLineSegment(sketch, "E51.13.0", {"start": v(10.58, 14.57) * mm, "end": v(11.3, 15.54) * mm});
            skLineSegment(sketch, "E51.13.1", {"start": v(14.24, 16.67) * mm, "end": v(14.34, 17.22) * mm});
            skLineSegment(sketch, "E51.13.2", {"start": v(12.33, 13.13) * mm, "end": v(13.15, 14) * mm});
            skLineSegment(sketch, "E51.13.3", {"start": v(14.12, 16.18) * mm, "end": v(14.24, 16.67) * mm});
            skLineSegment(sketch, "E51.13.4", {"start": v(13.25, 16.9) * mm, "end": v(13.7, 17.11) * mm});
            skLineSegment(sketch, "E51.13.5", {"start": v(13.7, 17.11) * mm, "end": v(14.22, 17.3) * mm});
            skLineSegment(sketch, "E51.13.6", {"start": v(14, 15.74) * mm, "end": v(14.12, 16.18) * mm});
            skLineSegment(sketch, "E51.13.7", {"start": v(14.41, 17.81) * mm, "end": v(14.47, 18.46) * mm});
            skLineSegment(sketch, "E51.13.8", {"start": v(13.87, 15.36) * mm, "end": v(14, 15.74) * mm});
            skLineSegment(sketch, "E51.13.9", {"start": v(14.8, 17.5) * mm, "end": v(15.42, 17.67) * mm});
            skLineSegment(sketch, "E51.13.10", {"start": v(14.34, 17.22) * mm, "end": v(14.41, 17.81) * mm});
            skLineSegment(sketch, "E51.13.11", {"start": v(12.84, 16.7) * mm, "end": v(13.25, 16.9) * mm});
            skLineSegment(sketch, "E51.13.12", {"start": v(14.22, 17.3) * mm, "end": v(14.8, 17.5) * mm});
            skLineSegment(sketch, "E51.13.13", {"start": v(13.48, 14.5) * mm, "end": v(13.6, 14.74) * mm});
            skLineSegment(sketch, "E51.13.14", {"start": v(13.6, 14.74) * mm, "end": v(13.73, 15.02) * mm});
            skLineSegment(sketch, "E51.13.15", {"start": v(13.73, 15.02) * mm, "end": v(13.87, 15.36) * mm});
            skLineSegment(sketch, "E51.13.16", {"start": v(12.18, 16.3) * mm, "end": v(12.49, 16.5) * mm});
            skLineSegment(sketch, "E51.13.17", {"start": v(11.93, 16.13) * mm, "end": v(12.18, 16.3) * mm});
            skLineSegment(sketch, "E51.13.18", {"start": v(12.49, 16.5) * mm, "end": v(12.84, 16.7) * mm});
            skLineSegment(sketch, "E51.13.19", {"start": v(13.37, 14.32) * mm, "end": v(13.48, 14.5) * mm});
            skLineSegment(sketch, "E51.13.20", {"start": v(13.28, 14.18) * mm, "end": v(13.37, 14.32) * mm});
            skLineSegment(sketch, "E51.13.21", {"start": v(11.72, 15.96) * mm, "end": v(11.93, 16.13) * mm});
            skLineSegment(sketch, "E51.13.22", {"start": v(11.56, 15.82) * mm, "end": v(11.72, 15.96) * mm});
            skLineSegment(sketch, "E51.13.23", {"start": v(11.35, 15.62) * mm, "end": v(11.44, 15.7) * mm});
            skLineSegment(sketch, "E51.13.24", {"start": v(13.15, 14) * mm, "end": v(13.17, 14.02) * mm});
            skLineSegment(sketch, "E51.13.25", {"start": v(13.17, 14.02) * mm, "end": v(13.21, 14.08) * mm});
            skLineSegment(sketch, "E51.13.26", {"start": v(11.44, 15.7) * mm, "end": v(11.56, 15.82) * mm});
            skLineSegment(sketch, "E51.13.27", {"start": v(13.21, 14.08) * mm, "end": v(13.28, 14.18) * mm});
            skLineSegment(sketch, "E51.13.28", {"start": v(11.3, 15.56) * mm, "end": v(11.35, 15.62) * mm});
            skLineSegment(sketch, "E51.13.29", {"start": v(11.3, 15.54) * mm, "end": v(11.3, 15.56) * mm});
            skLineSegment(sketch, "E51.14.0", {"start": v(5.56, 17.13) * mm, "end": v(5.94, 18.27) * mm});
            skLineSegment(sketch, "E51.14.1", {"start": v(8.39, 20.26) * mm, "end": v(8.32, 20.8) * mm});
            skLineSegment(sketch, "E51.14.2", {"start": v(7.67, 16.3) * mm, "end": v(8.18, 17.38) * mm});
            skLineSegment(sketch, "E51.14.3", {"start": v(8.43, 19.75) * mm, "end": v(8.39, 20.26) * mm});
            skLineSegment(sketch, "E51.14.4", {"start": v(7.38, 20.17) * mm, "end": v(7.75, 20.51) * mm});
            skLineSegment(sketch, "E51.14.5", {"start": v(7.75, 20.51) * mm, "end": v(8.18, 20.86) * mm});
            skLineSegment(sketch, "E51.14.6", {"start": v(8.45, 19.3) * mm, "end": v(8.43, 19.75) * mm});
            skLineSegment(sketch, "E51.14.7", {"start": v(8.2, 21.4) * mm, "end": v(8.05, 22.02) * mm});
            skLineSegment(sketch, "E51.14.8", {"start": v(8.44, 18.9) * mm, "end": v(8.45, 19.3) * mm});
            skLineSegment(sketch, "E51.14.9", {"start": v(8.66, 21.21) * mm, "end": v(9.2, 21.57) * mm});
            skLineSegment(sketch, "E51.14.10", {"start": v(8.32, 20.8) * mm, "end": v(8.2, 21.4) * mm});
            skLineSegment(sketch, "E51.14.11", {"start": v(7.05, 19.85) * mm, "end": v(7.38, 20.17) * mm});
            skLineSegment(sketch, "E51.14.12", {"start": v(8.18, 20.86) * mm, "end": v(8.66, 21.21) * mm});
            skLineSegment(sketch, "E51.14.13", {"start": v(8.34, 17.96) * mm, "end": v(8.38, 18.22) * mm});
            skLineSegment(sketch, "E51.14.14", {"start": v(8.38, 18.22) * mm, "end": v(8.42, 18.53) * mm});
            skLineSegment(sketch, "E51.14.15", {"start": v(8.42, 18.53) * mm, "end": v(8.44, 18.9) * mm});
            skLineSegment(sketch, "E51.14.16", {"start": v(6.55, 19.27) * mm, "end": v(6.78, 19.55) * mm});
            skLineSegment(sketch, "E51.14.17", {"start": v(6.36, 19.02) * mm, "end": v(6.55, 19.27) * mm});
            skLineSegment(sketch, "E51.14.18", {"start": v(6.78, 19.55) * mm, "end": v(7.05, 19.85) * mm});
            skLineSegment(sketch, "E51.14.19", {"start": v(8.3, 17.75) * mm, "end": v(8.34, 17.96) * mm});
            skLineSegment(sketch, "E51.14.20", {"start": v(8.25, 17.59) * mm, "end": v(8.3, 17.75) * mm});
            skLineSegment(sketch, "E51.14.21", {"start": v(6.21, 18.8) * mm, "end": v(6.36, 19.02) * mm});
            skLineSegment(sketch, "E51.14.22", {"start": v(6.1, 18.62) * mm, "end": v(6.21, 18.8) * mm});
            skLineSegment(sketch, "E51.14.23", {"start": v(5.97, 18.36) * mm, "end": v(6.02, 18.47) * mm});
            skLineSegment(sketch, "E51.14.24", {"start": v(8.18, 17.38) * mm, "end": v(8.19, 17.4) * mm});
            skLineSegment(sketch, "E51.14.25", {"start": v(8.19, 17.4) * mm, "end": v(8.21, 17.47) * mm});
            skLineSegment(sketch, "E51.14.26", {"start": v(6.02, 18.47) * mm, "end": v(6.1, 18.62) * mm});
            skLineSegment(sketch, "E51.14.27", {"start": v(8.21, 17.47) * mm, "end": v(8.25, 17.59) * mm});
            skLineSegment(sketch, "E51.14.28", {"start": v(5.94, 18.3) * mm, "end": v(5.97, 18.36) * mm});
            skLineSegment(sketch, "E51.14.29", {"start": v(5.94, 18.27) * mm, "end": v(5.94, 18.3) * mm});
            skLineSegment(sketch, "E51.15.0", {"start": v(0, 18) * mm, "end": v(0, 19.21) * mm});
            skLineSegment(sketch, "E51.15.1", {"start": v(1.72, 21.86) * mm, "end": v(1.48, 22.36) * mm});
            skLineSegment(sketch, "E51.15.2", {"start": v(2.26, 17.87) * mm, "end": v(2.4, 19.06) * mm});
            skLineSegment(sketch, "E51.15.3", {"start": v(1.92, 21.4) * mm, "end": v(1.72, 21.86) * mm});
            skLineSegment(sketch, "E51.15.4", {"start": v(0.78, 21.47) * mm, "end": v(1.03, 21.9) * mm});
            skLineSegment(sketch, "E51.15.5", {"start": v(1.03, 21.9) * mm, "end": v(1.33, 22.36) * mm});
            skLineSegment(sketch, "E51.15.6", {"start": v(2.07, 20.97) * mm, "end": v(1.92, 21.4) * mm});
            skLineSegment(sketch, "E51.15.7", {"start": v(1.2, 22.88) * mm, "end": v(0.85, 23.44) * mm});
            skLineSegment(sketch, "E51.15.8", {"start": v(2.2, 20.58) * mm, "end": v(2.07, 20.97) * mm});
            skLineSegment(sketch, "E51.15.9", {"start": v(1.69, 22.85) * mm, "end": v(2.1, 23.36) * mm});
            skLineSegment(sketch, "E51.15.10", {"start": v(1.48, 22.36) * mm, "end": v(1.2, 22.88) * mm});
            skLineSegment(sketch, "E51.15.11", {"start": v(0.57, 21.06) * mm, "end": v(0.78, 21.47) * mm});
            skLineSegment(sketch, "E51.15.12", {"start": v(1.33, 22.36) * mm, "end": v(1.69, 22.85) * mm});
            skLineSegment(sketch, "E51.15.13", {"start": v(2.38, 19.66) * mm, "end": v(2.34, 19.92) * mm});
            skLineSegment(sketch, "E51.15.14", {"start": v(2.34, 19.92) * mm, "end": v(2.28, 20.23) * mm});
            skLineSegment(sketch, "E51.15.15", {"start": v(2.28, 20.23) * mm, "end": v(2.2, 20.58) * mm});
            skLineSegment(sketch, "E51.15.16", {"start": v(0.27, 20.35) * mm, "end": v(0.4, 20.69) * mm});
            skLineSegment(sketch, "E51.15.17", {"start": v(0.17, 20.06) * mm, "end": v(0.27, 20.35) * mm});
            skLineSegment(sketch, "E51.15.18", {"start": v(0.4, 20.69) * mm, "end": v(0.57, 21.06) * mm});
            skLineSegment(sketch, "E51.15.19", {"start": v(2.4, 19.44) * mm, "end": v(2.38, 19.66) * mm});
            skLineSegment(sketch, "E51.15.20", {"start": v(2.41, 19.28) * mm, "end": v(2.4, 19.44) * mm});
            skLineSegment(sketch, "E51.15.21", {"start": v(0.1, 19.8) * mm, "end": v(0.17, 20.06) * mm});
            skLineSegment(sketch, "E51.15.22", {"start": v(0.05, 19.6) * mm, "end": v(0.1, 19.8) * mm});
            skLineSegment(sketch, "E51.15.23", {"start": v(0, 19.3) * mm, "end": v(0.02, 19.43) * mm});
            skLineSegment(sketch, "E51.15.24", {"start": v(2.4, 19.06) * mm, "end": v(2.41, 19.08) * mm});
            skLineSegment(sketch, "E51.15.25", {"start": v(2.41, 19.08) * mm, "end": v(2.41, 19.16) * mm});
            skLineSegment(sketch, "E51.15.26", {"start": v(0.02, 19.43) * mm, "end": v(0.05, 19.6) * mm});
            skLineSegment(sketch, "E51.15.27", {"start": v(2.41, 19.16) * mm, "end": v(2.41, 19.28) * mm});
            skLineSegment(sketch, "E51.15.28", {"start": v(0, 19.24) * mm, "end": v(0, 19.3) * mm});
            skLineSegment(sketch, "E51.15.29", {"start": v(0, 19.21) * mm, "end": v(0, 19.24) * mm});
            skLineSegment(sketch, "E51.16.0", {"start": v(-5.56, 17.13) * mm, "end": v(-5.94, 18.27) * mm});
            skLineSegment(sketch, "E51.16.1", {"start": v(-5.12, 21.32) * mm, "end": v(-5.5, 21.72) * mm});
            skLineSegment(sketch, "E51.16.2", {"start": v(-3.37, 17.69) * mm, "end": v(-3.6, 18.87) * mm});
            skLineSegment(sketch, "E51.16.3", {"start": v(-4.79, 20.94) * mm, "end": v(-5.12, 21.32) * mm});
            skLineSegment(sketch, "E51.16.4", {"start": v(-5.9, 20.66) * mm, "end": v(-5.78, 21.15) * mm});
            skLineSegment(sketch, "E51.16.5", {"start": v(-5.78, 21.15) * mm, "end": v(-5.64, 21.68) * mm});
            skLineSegment(sketch, "E51.16.6", {"start": v(-4.5, 20.58) * mm, "end": v(-4.79, 20.94) * mm});
            skLineSegment(sketch, "E51.16.7", {"start": v(-5.94, 22.13) * mm, "end": v(-6.43, 22.55) * mm});
            skLineSegment(sketch, "E51.16.8", {"start": v(-4.27, 20.25) * mm, "end": v(-4.5, 20.58) * mm});
            skLineSegment(sketch, "E51.16.9", {"start": v(-5.46, 22.25) * mm, "end": v(-5.23, 22.86) * mm});
            skLineSegment(sketch, "E51.16.10", {"start": v(-5.5, 21.72) * mm, "end": v(-5.94, 22.13) * mm});
            skLineSegment(sketch, "E51.16.11", {"start": v(-5.96, 20.2) * mm, "end": v(-5.9, 20.66) * mm});
            skLineSegment(sketch, "E51.16.12", {"start": v(-5.64, 21.68) * mm, "end": v(-5.46, 22.25) * mm});
            skLineSegment(sketch, "E51.16.13", {"start": v(-3.8, 19.43) * mm, "end": v(-3.93, 19.67) * mm});
            skLineSegment(sketch, "E51.16.14", {"start": v(-3.93, 19.67) * mm, "end": v(-4.08, 19.94) * mm});
            skLineSegment(sketch, "E51.16.15", {"start": v(-4.08, 19.94) * mm, "end": v(-4.27, 20.25) * mm});
            skLineSegment(sketch, "E51.16.16", {"start": v(-6.03, 19.44) * mm, "end": v(-6, 19.8) * mm});
            skLineSegment(sketch, "E51.16.17", {"start": v(-6.03, 19.13) * mm, "end": v(-6.03, 19.44) * mm});
            skLineSegment(sketch, "E51.16.18", {"start": v(-6, 19.8) * mm, "end": v(-5.96, 20.2) * mm});
            skLineSegment(sketch, "E51.16.19", {"start": v(-3.72, 19.24) * mm, "end": v(-3.8, 19.43) * mm});
            skLineSegment(sketch, "E51.16.20", {"start": v(-3.66, 19.08) * mm, "end": v(-3.72, 19.24) * mm});
            skLineSegment(sketch, "E51.16.21", {"start": v(-6.02, 18.86) * mm, "end": v(-6.03, 19.13) * mm});
            skLineSegment(sketch, "E51.16.22", {"start": v(-6, 18.65) * mm, "end": v(-6.02, 18.86) * mm});
            skLineSegment(sketch, "E51.16.23", {"start": v(-5.96, 18.36) * mm, "end": v(-5.98, 18.48) * mm});
            skLineSegment(sketch, "E51.16.24", {"start": v(-3.6, 18.87) * mm, "end": v(-3.6, 18.9) * mm});
            skLineSegment(sketch, "E51.16.25", {"start": v(-3.6, 18.9) * mm, "end": v(-3.62, 18.96) * mm});
            skLineSegment(sketch, "E51.16.26", {"start": v(-5.98, 18.48) * mm, "end": v(-6, 18.65) * mm});
            skLineSegment(sketch, "E51.16.27", {"start": v(-3.62, 18.96) * mm, "end": v(-3.66, 19.08) * mm});
            skLineSegment(sketch, "E51.16.28", {"start": v(-5.94, 18.3) * mm, "end": v(-5.96, 18.36) * mm});
            skLineSegment(sketch, "E51.16.29", {"start": v(-5.94, 18.27) * mm, "end": v(-5.94, 18.3) * mm});
            skLineSegment(sketch, "E51.17.0", {"start": v(-10.58, 14.57) * mm, "end": v(-11.3, 15.54) * mm});
            skLineSegment(sketch, "E51.17.1", {"start": v(-11.46, 18.7) * mm, "end": v(-11.94, 18.96) * mm});
            skLineSegment(sketch, "E51.17.2", {"start": v(-8.67, 15.78) * mm, "end": v(-9.26, 16.84) * mm});
            skLineSegment(sketch, "E51.17.3", {"start": v(-11.02, 18.43) * mm, "end": v(-11.46, 18.7) * mm});
            skLineSegment(sketch, "E51.17.4", {"start": v(-11.99, 17.82) * mm, "end": v(-12.04, 18.33) * mm});
            skLineSegment(sketch, "E51.17.5", {"start": v(-12.04, 18.33) * mm, "end": v(-12.07, 18.88) * mm});
            skLineSegment(sketch, "E51.17.6", {"start": v(-10.65, 18.18) * mm, "end": v(-11.02, 18.43) * mm});
            skLineSegment(sketch, "E51.17.7", {"start": v(-12.49, 19.21) * mm, "end": v(-13.08, 19.46) * mm});
            skLineSegment(sketch, "E51.17.8", {"start": v(-10.32, 17.93) * mm, "end": v(-10.65, 18.18) * mm});
            skLineSegment(sketch, "E51.17.9", {"start": v(-12.07, 19.48) * mm, "end": v(-12.04, 20.13) * mm});
            skLineSegment(sketch, "E51.17.10", {"start": v(-11.94, 18.96) * mm, "end": v(-12.49, 19.21) * mm});
            skLineSegment(sketch, "E51.17.11", {"start": v(-11.92, 17.37) * mm, "end": v(-11.99, 17.82) * mm});
            skLineSegment(sketch, "E51.17.12", {"start": v(-12.07, 18.88) * mm, "end": v(-12.07, 19.48) * mm});
            skLineSegment(sketch, "E51.17.13", {"start": v(-9.63, 17.3) * mm, "end": v(-9.81, 17.5) * mm});
            skLineSegment(sketch, "E51.17.14", {"start": v(-9.81, 17.5) * mm, "end": v(-10.04, 17.7) * mm});
            skLineSegment(sketch, "E51.17.15", {"start": v(-10.04, 17.7) * mm, "end": v(-10.32, 17.93) * mm});
            skLineSegment(sketch, "E51.17.16", {"start": v(-11.74, 16.63) * mm, "end": v(-11.83, 16.97) * mm});
            skLineSegment(sketch, "E51.17.17", {"start": v(-11.65, 16.33) * mm, "end": v(-11.74, 16.63) * mm});
            skLineSegment(sketch, "E51.17.18", {"start": v(-11.83, 16.97) * mm, "end": v(-11.92, 17.37) * mm});
            skLineSegment(sketch, "E51.17.19", {"start": v(-9.48, 17.14) * mm, "end": v(-9.63, 17.3) * mm});
            skLineSegment(sketch, "E51.17.20", {"start": v(-9.38, 17.01) * mm, "end": v(-9.48, 17.14) * mm});
            skLineSegment(sketch, "E51.17.21", {"start": v(-11.56, 16.08) * mm, "end": v(-11.65, 16.33) * mm});
            skLineSegment(sketch, "E51.17.22", {"start": v(-11.47, 15.88) * mm, "end": v(-11.56, 16.08) * mm});
            skLineSegment(sketch, "E51.17.23", {"start": v(-11.34, 15.62) * mm, "end": v(-11.4, 15.73) * mm});
            skLineSegment(sketch, "E51.17.24", {"start": v(-9.26, 16.84) * mm, "end": v(-9.27, 16.86) * mm});
            skLineSegment(sketch, "E51.17.25", {"start": v(-9.27, 16.86) * mm, "end": v(-9.3, 16.92) * mm});
            skLineSegment(sketch, "E51.17.26", {"start": v(-11.4, 15.73) * mm, "end": v(-11.47, 15.88) * mm});
            skLineSegment(sketch, "E51.17.27", {"start": v(-9.3, 16.92) * mm, "end": v(-9.38, 17.01) * mm});
            skLineSegment(sketch, "E51.17.28", {"start": v(-11.3, 15.56) * mm, "end": v(-11.34, 15.62) * mm});
            skLineSegment(sketch, "E51.17.29", {"start": v(-11.3, 15.54) * mm, "end": v(-11.3, 15.56) * mm});
            skLineSegment(sketch, "E51.18.0", {"start": v(-14.57, 10.58) * mm, "end": v(-15.54, 11.3) * mm});
            skLineSegment(sketch, "E51.18.1", {"start": v(-16.67, 14.24) * mm, "end": v(-17.22, 14.34) * mm});
            skLineSegment(sketch, "E51.18.2", {"start": v(-13.13, 12.33) * mm, "end": v(-14, 13.15) * mm});
            skLineSegment(sketch, "E51.18.3", {"start": v(-16.18, 14.12) * mm, "end": v(-16.67, 14.24) * mm});
            skLineSegment(sketch, "E51.18.4", {"start": v(-16.9, 13.25) * mm, "end": v(-17.11, 13.7) * mm});
            skLineSegment(sketch, "E51.18.5", {"start": v(-17.11, 13.7) * mm, "end": v(-17.3, 14.22) * mm});
            skLineSegment(sketch, "E51.18.6", {"start": v(-15.74, 14) * mm, "end": v(-16.18, 14.12) * mm});
            skLineSegment(sketch, "E51.18.7", {"start": v(-17.81, 14.41) * mm, "end": v(-18.46, 14.47) * mm});
            skLineSegment(sketch, "E51.18.8", {"start": v(-15.36, 13.87) * mm, "end": v(-15.74, 14) * mm});
            skLineSegment(sketch, "E51.18.9", {"start": v(-17.5, 14.8) * mm, "end": v(-17.67, 15.42) * mm});
            skLineSegment(sketch, "E51.18.10", {"start": v(-17.22, 14.34) * mm, "end": v(-17.81, 14.41) * mm});
            skLineSegment(sketch, "E51.18.11", {"start": v(-16.7, 12.84) * mm, "end": v(-16.9, 13.25) * mm});
            skLineSegment(sketch, "E51.18.12", {"start": v(-17.3, 14.22) * mm, "end": v(-17.5, 14.8) * mm});
            skLineSegment(sketch, "E51.18.13", {"start": v(-14.5, 13.48) * mm, "end": v(-14.74, 13.6) * mm});
            skLineSegment(sketch, "E51.18.14", {"start": v(-14.74, 13.6) * mm, "end": v(-15.02, 13.73) * mm});
            skLineSegment(sketch, "E51.18.15", {"start": v(-15.02, 13.73) * mm, "end": v(-15.36, 13.87) * mm});
            skLineSegment(sketch, "E51.18.16", {"start": v(-16.3, 12.18) * mm, "end": v(-16.5, 12.49) * mm});
            skLineSegment(sketch, "E51.18.17", {"start": v(-16.13, 11.93) * mm, "end": v(-16.3, 12.18) * mm});
            skLineSegment(sketch, "E51.18.18", {"start": v(-16.5, 12.49) * mm, "end": v(-16.7, 12.84) * mm});
            skLineSegment(sketch, "E51.18.19", {"start": v(-14.32, 13.37) * mm, "end": v(-14.5, 13.48) * mm});
            skLineSegment(sketch, "E51.18.20", {"start": v(-14.18, 13.28) * mm, "end": v(-14.32, 13.37) * mm});
            skLineSegment(sketch, "E51.18.21", {"start": v(-15.96, 11.72) * mm, "end": v(-16.13, 11.93) * mm});
            skLineSegment(sketch, "E51.18.22", {"start": v(-15.82, 11.56) * mm, "end": v(-15.96, 11.72) * mm});
            skLineSegment(sketch, "E51.18.23", {"start": v(-15.62, 11.35) * mm, "end": v(-15.7, 11.44) * mm});
            skLineSegment(sketch, "E51.18.24", {"start": v(-14, 13.15) * mm, "end": v(-14.02, 13.17) * mm});
            skLineSegment(sketch, "E51.18.25", {"start": v(-14.02, 13.17) * mm, "end": v(-14.08, 13.21) * mm});
            skLineSegment(sketch, "E51.18.26", {"start": v(-15.7, 11.44) * mm, "end": v(-15.82, 11.56) * mm});
            skLineSegment(sketch, "E51.18.27", {"start": v(-14.08, 13.21) * mm, "end": v(-14.18, 13.28) * mm});
            skLineSegment(sketch, "E51.18.28", {"start": v(-15.56, 11.3) * mm, "end": v(-15.62, 11.35) * mm});
            skLineSegment(sketch, "E51.18.29", {"start": v(-15.54, 11.3) * mm, "end": v(-15.56, 11.3) * mm});
            skLineSegment(sketch, "E51.19.0", {"start": v(-17.13, 5.56) * mm, "end": v(-18.27, 5.94) * mm});
            skLineSegment(sketch, "E51.19.1", {"start": v(-20.26, 8.39) * mm, "end": v(-20.8, 8.32) * mm});
            skLineSegment(sketch, "E51.19.2", {"start": v(-16.3, 7.67) * mm, "end": v(-17.38, 8.18) * mm});
            skLineSegment(sketch, "E51.19.3", {"start": v(-19.75, 8.43) * mm, "end": v(-20.26, 8.39) * mm});
            skLineSegment(sketch, "E51.19.4", {"start": v(-20.17, 7.38) * mm, "end": v(-20.51, 7.75) * mm});
            skLineSegment(sketch, "E51.19.5", {"start": v(-20.51, 7.75) * mm, "end": v(-20.86, 8.18) * mm});
            skLineSegment(sketch, "E51.19.6", {"start": v(-19.3, 8.45) * mm, "end": v(-19.75, 8.43) * mm});
            skLineSegment(sketch, "E51.19.7", {"start": v(-21.4, 8.2) * mm, "end": v(-22.02, 8.05) * mm});
            skLineSegment(sketch, "E51.19.8", {"start": v(-18.9, 8.44) * mm, "end": v(-19.3, 8.45) * mm});
            skLineSegment(sketch, "E51.19.9", {"start": v(-21.21, 8.66) * mm, "end": v(-21.57, 9.2) * mm});
            skLineSegment(sketch, "E51.19.10", {"start": v(-20.8, 8.32) * mm, "end": v(-21.4, 8.2) * mm});
            skLineSegment(sketch, "E51.19.11", {"start": v(-19.85, 7.05) * mm, "end": v(-20.17, 7.38) * mm});
            skLineSegment(sketch, "E51.19.12", {"start": v(-20.86, 8.18) * mm, "end": v(-21.21, 8.66) * mm});
            skLineSegment(sketch, "E51.19.13", {"start": v(-17.96, 8.34) * mm, "end": v(-18.22, 8.38) * mm});
            skLineSegment(sketch, "E51.19.14", {"start": v(-18.22, 8.38) * mm, "end": v(-18.53, 8.42) * mm});
            skLineSegment(sketch, "E51.19.15", {"start": v(-18.53, 8.42) * mm, "end": v(-18.9, 8.44) * mm});
            skLineSegment(sketch, "E51.19.16", {"start": v(-19.27, 6.55) * mm, "end": v(-19.55, 6.78) * mm});
            skLineSegment(sketch, "E51.19.17", {"start": v(-19.02, 6.36) * mm, "end": v(-19.27, 6.55) * mm});
            skLineSegment(sketch, "E51.19.18", {"start": v(-19.55, 6.78) * mm, "end": v(-19.85, 7.05) * mm});
            skLineSegment(sketch, "E51.19.19", {"start": v(-17.75, 8.3) * mm, "end": v(-17.96, 8.34) * mm});
            skLineSegment(sketch, "E51.19.20", {"start": v(-17.59, 8.25) * mm, "end": v(-17.75, 8.3) * mm});
            skLineSegment(sketch, "E51.19.21", {"start": v(-18.8, 6.21) * mm, "end": v(-19.02, 6.36) * mm});
            skLineSegment(sketch, "E51.19.22", {"start": v(-18.62, 6.1) * mm, "end": v(-18.8, 6.21) * mm});
            skLineSegment(sketch, "E51.19.23", {"start": v(-18.36, 5.97) * mm, "end": v(-18.47, 6.02) * mm});
            skLineSegment(sketch, "E51.19.24", {"start": v(-17.38, 8.18) * mm, "end": v(-17.4, 8.19) * mm});
            skLineSegment(sketch, "E51.19.25", {"start": v(-17.4, 8.19) * mm, "end": v(-17.47, 8.21) * mm});
            skLineSegment(sketch, "E51.19.26", {"start": v(-18.47, 6.02) * mm, "end": v(-18.62, 6.1) * mm});
            skLineSegment(sketch, "E51.19.27", {"start": v(-17.47, 8.21) * mm, "end": v(-17.59, 8.25) * mm});
            skLineSegment(sketch, "E51.19.28", {"start": v(-18.3, 5.94) * mm, "end": v(-18.36, 5.97) * mm});
            skLineSegment(sketch, "E51.19.29", {"start": v(-18.27, 5.94) * mm, "end": v(-18.3, 5.94) * mm});
            skSolve(sketch);
        }
        {
            var Q0;
            {var subQ0=sQuery(id+"F1.wireOp",EDGE,"E0");var subQ27=makeQuery(id+"F1.imprint","INTERSECT",VERTEX,{"derivedFrom":[subQ0,sQuery(id+"F1.wireOp",EDGE,"E51.10.0")]});Q0=makeQuery(id+"F1.imprint","IMPRINT",FACE,{"disambiguationData":[TD([[makeQuery(id+"F1.imprint","IMPRINT",EDGE,{"disambiguationData":[TD([[subQ27,-1.0]])],"derivedFrom":subQ0}),1.0]])]});}
            var Q1;
            {var subQ0=sQuery(id+"F1.wireOp",EDGE,"E51.1.0");Q1=makeQuery(id+"F1.imprint","IMPRINT",FACE,{"disambiguationData":[TD([[makeQuery(id+"F1.imprint","IMPRINT",EDGE,{"derivedFrom":subQ0}),-1.0]])]});}
            var Q2;
            {var subQ7=sQuery(id+"F1.wireOp",EDGE,"E51.2.0");Q2=makeQuery(id+"F1.imprint","IMPRINT",FACE,{"disambiguationData":[TD([[makeQuery(id+"F1.imprint","IMPRINT",EDGE,{"derivedFrom":subQ7}),-1.0]])]});}
            var Q3;
            {var subQ8=sQuery(id+"F1.wireOp",EDGE,"E51.3.0");Q3=makeQuery(id+"F1.imprint","IMPRINT",FACE,{"disambiguationData":[TD([[makeQuery(id+"F1.imprint","IMPRINT",EDGE,{"derivedFrom":subQ8}),-1.0]])]});}
            var Q4;
            {var subQ2=sQuery(id+"F1.wireOp",EDGE,"E51.4.0");Q4=makeQuery(id+"F1.imprint","IMPRINT",FACE,{"disambiguationData":[TD([[makeQuery(id+"F1.imprint","IMPRINT",EDGE,{"derivedFrom":subQ2}),-1.0]])]});}
            var Q5;
            {var subQ8=sQuery(id+"F1.wireOp",EDGE,"E51.5.0");Q5=makeQuery(id+"F1.imprint","IMPRINT",FACE,{"disambiguationData":[TD([[makeQuery(id+"F1.imprint","IMPRINT",EDGE,{"derivedFrom":subQ8}),-1.0]])]});}
            var Q6;
            {var subQ3=sQuery(id+"F1.wireOp",EDGE,"E51.6.0");Q6=makeQuery(id+"F1.imprint","IMPRINT",FACE,{"disambiguationData":[TD([[makeQuery(id+"F1.imprint","IMPRINT",EDGE,{"derivedFrom":subQ3}),-1.0]])]});}
            var Q7;
            {var subQ0=sQuery(id+"F1.wireOp",EDGE,"E51.7.0");Q7=makeQuery(id+"F1.imprint","IMPRINT",FACE,{"disambiguationData":[TD([[makeQuery(id+"F1.imprint","IMPRINT",EDGE,{"derivedFrom":subQ0}),-1.0]])]});}
            var Q8;
            {var subQ5=sQuery(id+"F1.wireOp",EDGE,"E51.8.0");Q8=makeQuery(id+"F1.imprint","IMPRINT",FACE,{"disambiguationData":[TD([[makeQuery(id+"F1.imprint","IMPRINT",EDGE,{"derivedFrom":subQ5}),-1.0]])]});}
            var Q9;
            {var subQ1=sQuery(id+"F1.wireOp",EDGE,"E51.9.0");Q9=makeQuery(id+"F1.imprint","IMPRINT",FACE,{"disambiguationData":[TD([[makeQuery(id+"F1.imprint","IMPRINT",EDGE,{"derivedFrom":subQ1}),-1.0]])]});}
            var Q10;
            {var subQ5=sQuery(id+"F1.wireOp",EDGE,"E51.10.0");Q10=makeQuery(id+"F1.imprint","IMPRINT",FACE,{"disambiguationData":[TD([[makeQuery(id+"F1.imprint","IMPRINT",EDGE,{"derivedFrom":subQ5}),-1.0]])]});}
            var Q11;
            {var subQ8=sQuery(id+"F1.wireOp",EDGE,"E51.11.0");Q11=makeQuery(id+"F1.imprint","IMPRINT",FACE,{"disambiguationData":[TD([[makeQuery(id+"F1.imprint","IMPRINT",EDGE,{"derivedFrom":subQ8}),-1.0]])]});}
            var Q12;
            {var subQ2=sQuery(id+"F1.wireOp",EDGE,"E51.12.0");Q12=makeQuery(id+"F1.imprint","IMPRINT",FACE,{"disambiguationData":[TD([[makeQuery(id+"F1.imprint","IMPRINT",EDGE,{"derivedFrom":subQ2}),-1.0]])]});}
            var Q13;
            {var subQ3=sQuery(id+"F1.wireOp",EDGE,"E51.13.0");Q13=makeQuery(id+"F1.imprint","IMPRINT",FACE,{"disambiguationData":[TD([[makeQuery(id+"F1.imprint","IMPRINT",EDGE,{"derivedFrom":subQ3}),-1.0]])]});}
            var Q14;
            {var subQ0=sQuery(id+"F1.wireOp",EDGE,"E51.14.0");Q14=makeQuery(id+"F1.imprint","IMPRINT",FACE,{"disambiguationData":[TD([[makeQuery(id+"F1.imprint","IMPRINT",EDGE,{"derivedFrom":subQ0}),-1.0]])]});}
            var Q15;
            {var subQ6=sQuery(id+"F1.wireOp",EDGE,"E51.15.0");Q15=makeQuery(id+"F1.imprint","IMPRINT",FACE,{"disambiguationData":[TD([[makeQuery(id+"F1.imprint","IMPRINT",EDGE,{"derivedFrom":subQ6}),-1.0]])]});}
            var Q16;
            {var subQ5=sQuery(id+"F1.wireOp",EDGE,"E51.16.0");Q16=makeQuery(id+"F1.imprint","IMPRINT",FACE,{"disambiguationData":[TD([[makeQuery(id+"F1.imprint","IMPRINT",EDGE,{"derivedFrom":subQ5}),-1.0]])]});}
            var Q17;
            {var subQ7=sQuery(id+"F1.wireOp",EDGE,"E51.17.0");Q17=makeQuery(id+"F1.imprint","IMPRINT",FACE,{"disambiguationData":[TD([[makeQuery(id+"F1.imprint","IMPRINT",EDGE,{"derivedFrom":subQ7}),-1.0]])]});}
            var Q18;
            {var subQ5=sQuery(id+"F1.wireOp",EDGE,"E51.18.0");Q18=makeQuery(id+"F1.imprint","IMPRINT",FACE,{"disambiguationData":[TD([[makeQuery(id+"F1.imprint","IMPRINT",EDGE,{"derivedFrom":subQ5}),-1.0]])]});}
            var Q19;
            {var subQ8=sQuery(id+"F1.wireOp",EDGE,"E51.19.0");Q19=makeQuery(id+"F1.imprint","IMPRINT",FACE,{"disambiguationData":[TD([[makeQuery(id+"F1.imprint","IMPRINT",EDGE,{"derivedFrom":subQ8}),-1.0]])]});}
            var Q20;
            {var subQ8=sQuery(id+"F1.wireOp",EDGE,"E21");Q20=makeQuery(id+"F1.imprint","IMPRINT",FACE,{"disambiguationData":[TD([[makeQuery(id+"F1.imprint","IMPRINT",EDGE,{"derivedFrom":subQ8}),-1.0]])]});}
            extrude(context, id + "F2", {"entities" : qUnion([Q0, Q1, Q2, Q3, Q4, Q5, Q6, Q7, Q8, Q9, Q10, Q11, Q12, Q13, Q14, Q15, Q16, Q17, Q18, Q19, Q20]), "depth" : (getVariable(context, 'GearThickness')) * mm});
        }
    });
